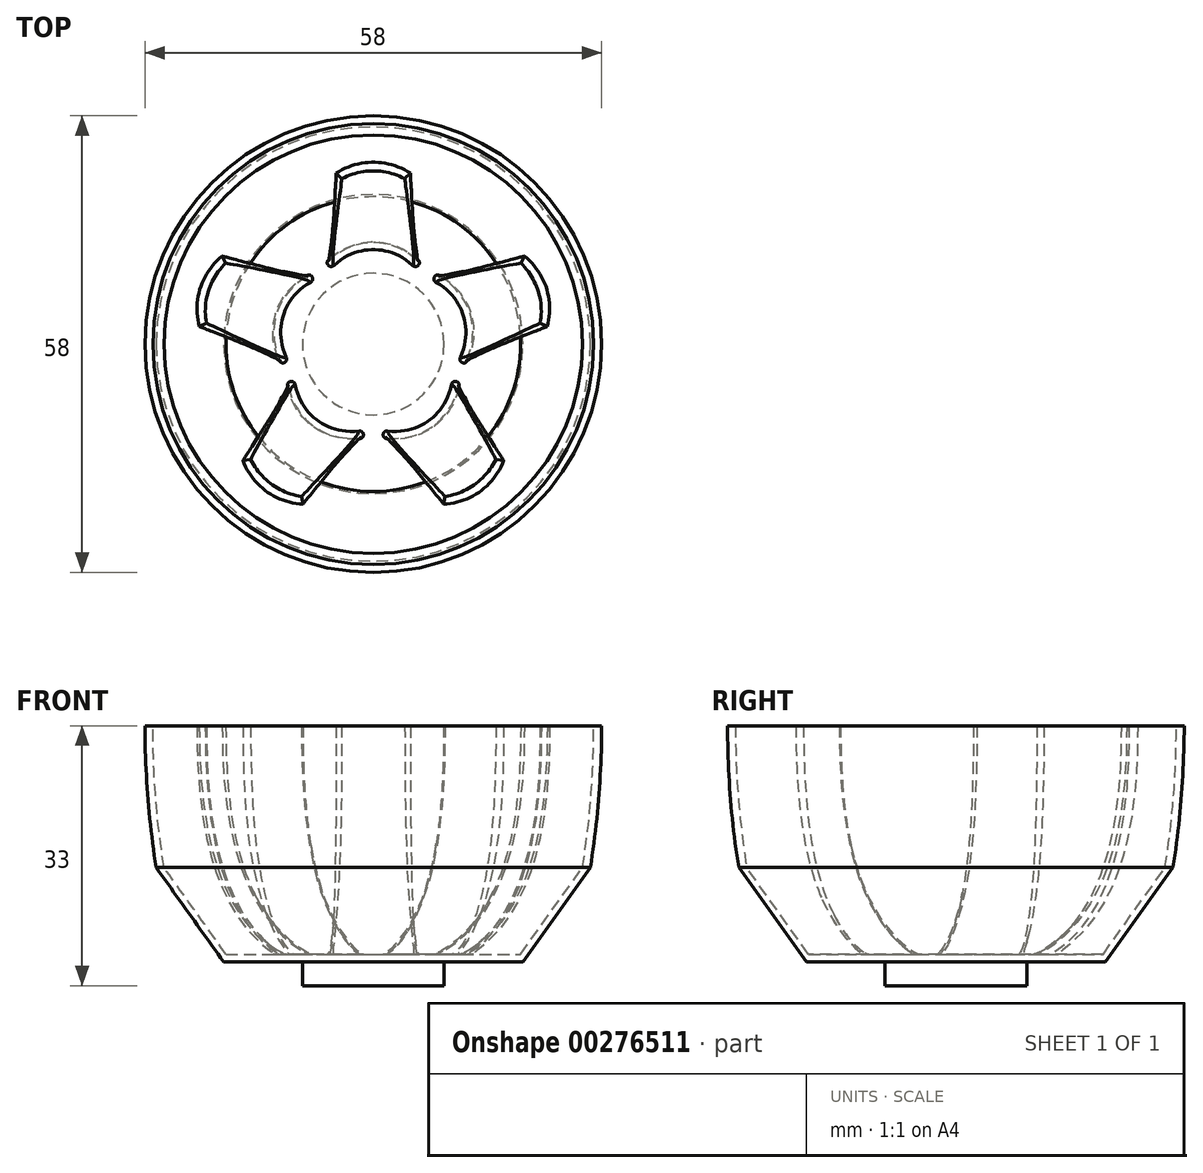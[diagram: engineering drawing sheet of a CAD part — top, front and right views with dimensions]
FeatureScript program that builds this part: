
annotation { "Feature Type Name" : "Feature", "Feature Type Description" : "" }
export const myFeature = defineFeature(function(context is Context, id is Id, definition is map)
    precondition{}
    {
        {
            var Q0;
            Q0=qCreatedBy(makeId("Right.planeOp"),FACE);
            var sketch = newSketch(context, id + "F0", { "sketchPlane" : qUnion([Q0])});
            skLineSegment(sketch, "E0", {"start": v(0, 0) * mm, "end": v(9, 0) * mm});
            skLineSegment(sketch, "E1", {"start": v(9, 0) * mm, "end": v(9, 3) * mm});
            skLineSegment(sketch, "E2", {"start": v(9, 3) * mm, "end": v(19, 3) * mm});
            skLineSegment(sketch, "E3", {"start": v(25, 63) * mm, "end": v(9, 63) * mm});
            skLineSegment(sketch, "E4", {"start": v(9, 63) * mm, "end": v(9, 66) * mm});
            skLineSegment(sketch, "E5", {"start": v(9, 66) * mm, "end": v(0, 66) * mm});
            skLineSegment(sketch, "E6", {"start": v(24.27, 62) * mm, "end": v(0, 62) * mm});
            skLineSegment(sketch, "E7", {"start": v(0, 62) * mm, "end": v(0, 66) * mm});
            skLineSegment(sketch, "E8", {"start": v(24.27, 4) * mm, "end": v(24, 4) * mm});
            skLineSegment(sketch, "E9", {"start": v(0, 4) * mm, "end": v(0, 0) * mm});
            skLineSegment(sketch, "E10", {"start": v(24, 3) * mm, "end": v(24, 33) * mm, "construction": true});
            skLineSegment(sketch, "E11", {"start": v(24, 33) * mm, "end": v(29, 33) * mm, "construction": true});
            skArc(sketch, "E12", {"start": v(27.58, 15) * mm, "mid": v(28.84, 39.14) * mm, "end": v(25, 63) * mm});
            skArc(sketch, "E13", {"start": v(26.58, 15) * mm, "mid": v(27.86, 38.62) * mm, "end": v(24.27, 62) * mm});
            skLineSegment(sketch, "E14", {"start": v(18.71, 4) * mm, "end": v(26.58, 15) * mm});
            skLineSegment(sketch, "E15.0", {"start": v(19, 3) * mm, "end": v(27.58, 15) * mm});
            skLineSegment(sketch, "E16.trimOffspring", {"start": v(24, 3) * mm, "end": v(25, 3) * mm});
            skLineSegment(sketch, "E17.trimOffspring", {"start": v(18.71, 4) * mm, "end": v(0, 4) * mm});
            skPoint(sketch, "E18.orphan", {"position": v(18, 3) * mm});
            skSolve(sketch);
        }
        {
            var Q0;
            {var subQ0=sQuery(id+"F0.wireOp",EDGE,"E4");Q0=makeQuery(id+"F0.imprint","IMPRINT",FACE,{"disambiguationData":[TD([[makeQuery(id+"F0.imprint","IMPRINT",EDGE,{"derivedFrom":subQ0}),1.0]])]});}
            var Q1;
            {var subQ0=sQuery(id+"F0.wireOp",EDGE,"Eq5XNbms-lTb5-H6kT-JK1Q-6tzkAojHCRK7");Q1=makeQuery(id+"F0.imprint","IMPRINT",FACE,{"disambiguationData":[TD([[makeQuery(id+"F0.imprint","IMPRINT",EDGE,{"derivedFrom":subQ0}),-1.0]])]});}
            var Q2;
            {var subQ0=sQuery(id+"F0.wireOp",EDGE,"UGsEUIsT-s4Y8-JkTt-294F-1TowYVN2bYvw");Q2=makeQuery(id+"F0.imprint","IMPRINT",FACE,{"disambiguationData":[TD([[makeQuery(id+"F0.imprint","IMPRINT",EDGE,{"derivedFrom":subQ0}),1.0]])]});}
            var Q3;
            {var subQ0=sQuery(id+"F0.wireOp",EDGE,"KxBa5Xhn-DWHx-Afoo-a3ch-oEYtl7JBiHtF");Q3=makeQuery(id+"F0.imprint","IMPRINT",FACE,{"disambiguationData":[TD([[makeQuery(id+"F0.imprint","IMPRINT",EDGE,{"derivedFrom":subQ0}),1.0]])]});}
            var Q4;
            Q4=makeQuery(id+"F0.imprint","IMPRINT",FACE,{"disambiguationData":[TD([[makeQuery(id+"F0.imprint","IMPRINT",EDGE,{"derivedFrom":sQuery(id+"F0.wireOp",EDGE,"E0")}),1.0]])]});
            var Q5;
            Q5=sQuery(id+"F0.wireOp",EDGE,"E7");
            revolve(context, id + "F1", {"entities" : qUnion([Q0, Q1, Q2, Q3, Q4]), "axis" : qUnion([Q5]), "revolveType" : RevolveType.FULL});
        }
        {
            var Q0;
            Q0=makeQuery(id+"F1.opRevolve","SWEPT_FACE",FACE,{"disambiguationData":[OSD([sQuery(id+"F0.wireOp",EDGE,"E5")])]});
            var sketch = newSketch(context, id + "F2", { "sketchPlane" : qUnion([Q0])});
            skLineSegment(sketch, "E19.bottom", {"start": v(44.27, 32.56) * mm, "end": v(-46.02, 32.56) * mm});
            skLineSegment(sketch, "E19.top", {"start": v(44.27, -32.56) * mm, "end": v(-46.02, -32.56) * mm});
            skLineSegment(sketch, "E19.left", {"start": v(44.27, 32.56) * mm, "end": v(44.27, -32.56) * mm});
            skLineSegment(sketch, "E19.right", {"start": v(-46.02, 32.56) * mm, "end": v(-46.02, -32.56) * mm});
            skPoint(sketch, "E19.middle", {"position": v(-0.88, 0) * mm});
            skSolve(sketch);
        }
        {
            var Q0;
            Q0=makeQuery(id+"F2.imprint","IMPRINT",FACE,{"disambiguationData":[TD([[makeQuery(id+"F2.imprint","IMPRINT",EDGE,{"derivedFrom":sQuery(id+"F2.wireOp",EDGE,"E19.bottom")}),1.0]])]});
            extrude(context, id + "F3", {"entities" : qUnion([Q0]), "operationType" : NewBodyOperationType.REMOVE, "oppositeDirection" : true, "depth" : 33 * mm});
        }
        {
            var Q0;
            Q0=makeQuery(id+"F1.opRevolve","SWEPT_FACE",FACE,{"disambiguationData":[OSD([sQuery(id+"F0.wireOp",EDGE,"E5")])]});
            extrude(context, id + "F4", {"entities" : qUnion([Q0]), "operationType" : NewBodyOperationType.REMOVE, "oppositeDirection" : true, "depth" : 25 * mm});
        }
        {
            var Q0;
            Q0=makeQuery(id+"F1.opRevolve","SWEPT_FACE",FACE,{"disambiguationData":[OSD([sQuery(id+"F0.wireOp",EDGE,"E17.trimOffspring")])]});
            var sketch = newSketch(context, id + "F5", { "sketchPlane" : qUnion([Q0])});
            skLineSegment(sketch, "E20", {"start": v(0, 0) * mm, "end": v(0, 10) * mm, "construction": true});
            skLineSegment(sketch, "E21", {"start": v(0, 10) * mm, "end": v(5, 10) * mm, "construction": true});
            skLineSegment(sketch, "E22", {"start": v(0, 10) * mm, "end": v(-5, 10) * mm, "construction": true});
            skLineSegment(sketch, "E23", {"start": v(-5, 10) * mm, "end": v(0, 10) * mm, "construction": true});
            skLineSegment(sketch, "E24", {"start": v(0, 10) * mm, "end": v(0, 12) * mm, "construction": true});
            skFitSpline(sketch, "E25", {"points": [v(-5, 10) * mm, v(0, 12) * mm, v(5, 10) * mm], "startDerivative": vector(10, 9) * mm, "endDerivative": vector(10, -9) * mm});
            skLineSegment(sketch, "E26", {"start": v(-5, 10) * mm, "end": v(-5.7, 10.7) * mm, "construction": true});
            skArc(sketch, "E27", {"start": v(-5.7, 10.7) * mm, "mid": v(-5.7, 10) * mm, "end": v(-5, 10) * mm});
            skLineSegment(sketch, "E28", {"start": v(0, 12) * mm, "end": v(0, 13) * mm, "construction": true});
            skArc(sketch, "E29.MirrorCS", {"start": v(5.7, 10.7) * mm, "mid": v(5.7, 10) * mm, "end": v(5, 10) * mm});
            skFitSpline(sketch, "E30", {"points": [v(-5.7, 10.7) * mm, v(0, 13) * mm, v(5.7, 10.7) * mm], "startDerivative": vector(10, 9) * mm, "endDerivative": vector(10, -9) * mm});
            skLineSegment(sketch, "E31", {"start": v(4.04, 12.2) * mm, "end": v(5.7, 10.7) * mm, "construction": true});
            skLineSegment(sketch, "E32", {"start": v(5, 10) * mm, "end": v(3.33, 11.5) * mm, "construction": true});
            skLineSegment(sketch, "E33", {"start": v(-5, 10) * mm, "end": v(-3.33, 11.5) * mm, "construction": true});
            skLineSegment(sketch, "E34", {"start": v(-4.04, 12.2) * mm, "end": v(-5.7, 10.7) * mm, "construction": true});
            skSolve(sketch);
        }
        {
            var Q0;
            Q0=makeQuery(id+"F3.boolean.opBoolean","COPY",FACE,{"derivedFrom":makeQuery(id+"F3.opExtrude","CAP_FACE",FACE,{"disambiguationData":[OSD([sQuery(id+"F0.wireOp",EDGE,"E4"),sQuery(id+"F0.wireOp",EDGE,"E5"),sQuery(id+"F2.wireOp",EDGE,"E19.bottom"),sQuery(id+"F2.wireOp",EDGE,"E19.top"),sQuery(id+"F2.wireOp",EDGE,"E19.left"),sQuery(id+"F2.wireOp",EDGE,"E19.right")])],"isStart":false})});
            var sketch = newSketch(context, id + "F6", { "sketchPlane" : qUnion([Q0])});
            skLineSegment(sketch, "E35", {"start": v(0, 0) * mm, "end": v(0, 22) * mm, "construction": true});
            skPoint(sketch, "E36.middle", {"position": v(0, 22) * mm});
            skLineSegment(sketch, "E37", {"start": v(0, 22) * mm, "end": v(0, 21) * mm, "construction": true});
            skLineSegment(sketch, "E38", {"start": v(0, 21) * mm, "end": v(4, 21) * mm, "construction": true});
            skLineSegment(sketch, "E39", {"start": v(0, 21) * mm, "end": v(-4, 21) * mm, "construction": true});
            skArc(sketch, "E40", {"start": v(4, 21) * mm, "mid": v(0, 22) * mm, "end": v(-4, 21) * mm});
            skLineSegment(sketch, "E41", {"start": v(4, 21) * mm, "end": v(4.7, 21.7) * mm});
            skLineSegment(sketch, "E42.MirrorCS", {"start": v(-4, 21) * mm, "end": v(-4.7, 21.7) * mm});
            skArc(sketch, "E43", {"start": v(4.7, 21.7) * mm, "mid": v(0, 23.1) * mm, "end": v(-4.7, 21.7) * mm});
            skSolve(sketch);
        }
        {
            var Q1;
            Q1=makeQuery(id+"F6.imprint","IMPRINT",FACE,{"disambiguationData":[TD([[makeQuery(id+"F6.imprint","IMPRINT",EDGE,{"derivedFrom":sQuery(id+"F6.wireOp",EDGE,"E40")}),-1.0]])]});
            var Q2;
            Q2=qSketchRegion(id+"F5",true);
            var Q3;
            Q3=sQuery(id+"Fp3v7k7kuvBsE9d_1.wireOp",EDGE,"ExajIc39-CtD1-VZ5m-11qJ-zfgL8IHDjS6G");
            loft(context, id + "F7", {"startCondition" : LoftEndDerivativeType.NORMAL_TO_PROFILE, "startMagnitude" : 3, "endCondition" : LoftEndDerivativeType.MATCH_CURVATURE, "endMagnitude" : 1, "sheetProfilesArray" : [{ "sheetProfileEntities" : qUnion([Q1]) }, { "sheetProfileEntities" : qUnion([Q2]) }], "guidesArray" : [{ "guideEntities" : qUnion([Q3]), "guideDerivativeType" : LoftGuideDerivativeType.DEFAULT, "guideDerivativeMagnitude" : 1 }]});
        }
        {
            var Q0;
            Q0=makeQuery(id+"F7.opLoft","SWEPT_BODY",BODY,{"disambiguationData":[OSD([makeQuery(id+"F5.imprint","IMPRINT",FACE,{"disambiguationData":[TD([[makeQuery(id+"F5.imprint","IMPRINT",EDGE,{"derivedFrom":sQuery(id+"F5.wireOp",EDGE,"E25")}),1.0]])]}),makeQuery(id+"F6.imprint","IMPRINT",FACE,{"disambiguationData":[TD([[makeQuery(id+"F6.imprint","IMPRINT",EDGE,{"derivedFrom":sQuery(id+"F6.wireOp",EDGE,"E40")}),-1.0]])]})])]});
            var Q1;
            Q1=sQuery(id+"F0.wireOp",EDGE,"E7");
            circularPattern(context, id + "F8", {"operationType" : NewBodyOperationType.ADD, "entities" : qUnion([Q0]), "axis" : qUnion([Q1]), "angle" : 360 * degree, "instanceCount" : 5, "equalSpace" : true});
        }
    });
